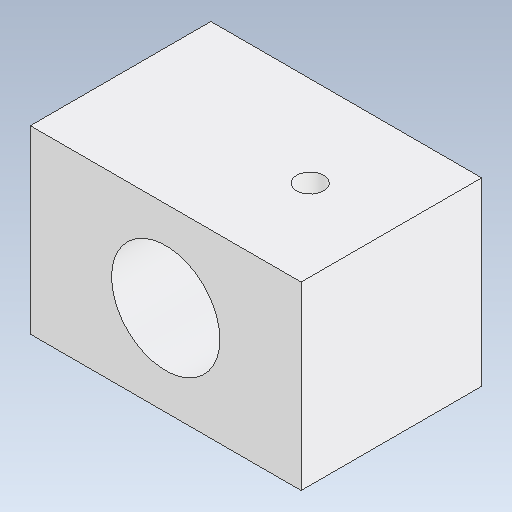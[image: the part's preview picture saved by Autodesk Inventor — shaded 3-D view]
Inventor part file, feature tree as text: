
AUTODESK INVENTOR PART (.ipt)
format: ipt  version: 2020.5 (Build 245400000, 400)  size: 112,128 bytes
history: native  units: mm
features: extrude x3, sketch x3
ambient origin geometry x8: Origin, YZ Plane, XZ Plane, XY Plane, X Axis, Y Axis, Z Axis, Center Point
bodies: Solid1 (feature_tree)
feature tree (6):
  extrude  "Extrusion1"  Depth=20.0mm
  sketch  "Sketch2"  dims[d0=12.0mm d1=20.0mm]
  extrude  "Extrusion2"  Depth=30.0mm
  extrude  "Extrusion3"  Depth=10.0mm
  sketch  "Sketch3"  dims[d2=20.0mm d3=0.0mm d4=30.0mm]
  sketch  "Sketch4"  dims[d5=10.0mm d6=0.0mm d7=3.0mm d8=10.0mm d9=0.0mm]
